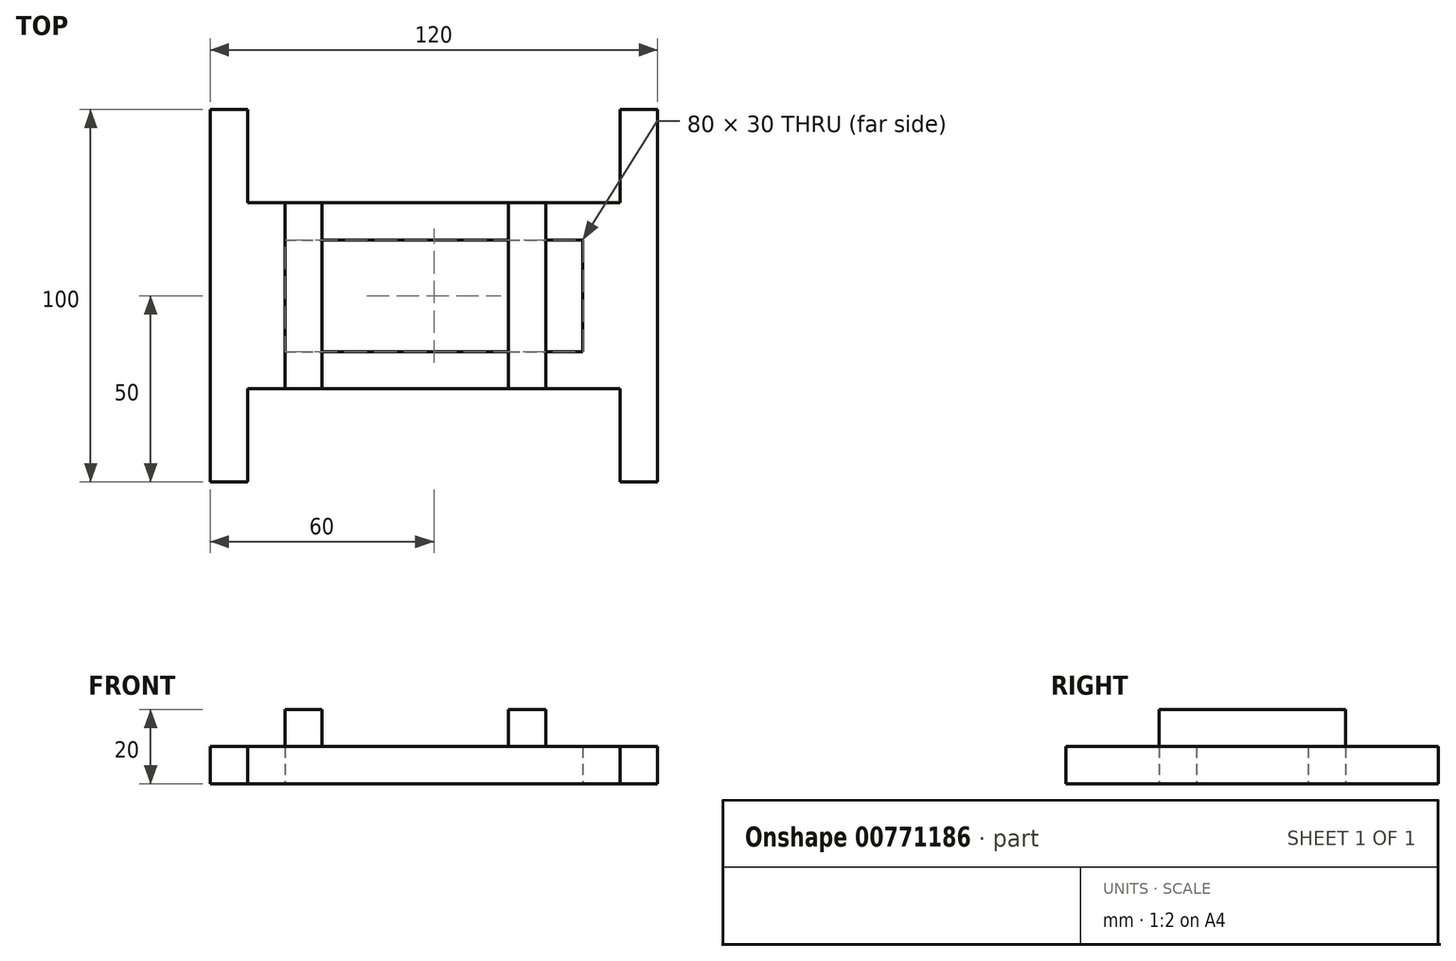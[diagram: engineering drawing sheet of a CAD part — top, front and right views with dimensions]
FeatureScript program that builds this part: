
annotation { "Feature Type Name" : "Feature", "Feature Type Description" : "" }
export const myFeature = defineFeature(function(context is Context, id is Id, definition is map)
    precondition{}
    {
        {
            var Q0;
            Q0=qCreatedBy(makeId("Top.planeOp"),FACE);
            var sketch = newSketch(context, id + "F0", { "sketchPlane" : qUnion([Q0])});
            skLineSegment(sketch, "E0.bottom", {"start": v(-50, 25) * mm, "end": v(50, 25) * mm});
            skLineSegment(sketch, "E0.top", {"start": v(-50, -25) * mm, "end": v(50, -25) * mm});
            skLineSegment(sketch, "E1.bottom", {"start": v(-60, 50) * mm, "end": v(-50, 50) * mm});
            skLineSegment(sketch, "E1.top", {"start": v(-60, -50) * mm, "end": v(-50, -50) * mm});
            skLineSegment(sketch, "E1.left", {"start": v(-60, 50) * mm, "end": v(-60, -50) * mm});
            skLineSegment(sketch, "E1.right", {"start": v(-50, 50) * mm, "end": v(-50, 25) * mm});
            skLineSegment(sketch, "E2.bottom", {"start": v(50, 50) * mm, "end": v(60, 50) * mm});
            skLineSegment(sketch, "E2.top", {"start": v(50, -50) * mm, "end": v(60, -50) * mm});
            skLineSegment(sketch, "E2.left", {"start": v(50, 50) * mm, "end": v(50, 25) * mm});
            skLineSegment(sketch, "E2.right", {"start": v(60, 50) * mm, "end": v(60, -50) * mm});
            skLineSegment(sketch, "E3.bottom", {"start": v(-40, 15) * mm, "end": v(40, 15) * mm});
            skLineSegment(sketch, "E3.top", {"start": v(-40, -15) * mm, "end": v(40, -15) * mm});
            skLineSegment(sketch, "E3.left", {"start": v(-40, 15) * mm, "end": v(-40, -15) * mm});
            skLineSegment(sketch, "E3.right", {"start": v(40, 15) * mm, "end": v(40, -15) * mm});
            skLineSegment(sketch, "E4.trimOffspring", {"start": v(-50, -25) * mm, "end": v(-50, -50) * mm});
            skLineSegment(sketch, "E5.trimOffspring", {"start": v(50, -25) * mm, "end": v(50, -50) * mm});
            skSolve(sketch);
        }
        {
            var Q0;
            Q0 = qSketchRegion(id + "F0", true);
            extrude(context, id + "F1", {"entities" : qUnion([Q0]), "depth" : 10 * mm, "offsetDistance" : 25 * mm});
        }
        {
            var Q0;
            Q0=makeQuery(id+"F1.opExtrude","SWEPT_FACE",FACE,{"disambiguationData":[OSD([sQuery(id+"F0.wireOp",EDGE,"E0.top")])]});
            var sketch = newSketch(context, id + "F2", { "sketchPlane" : qUnion([Q0])});
            skLineSegment(sketch, "E6.top", {"start": v(-50, 10) * mm, "end": v(-40, 10) * mm});
            skLineSegment(sketch, "E7.bottom", {"start": v(20, 20) * mm, "end": v(30, 20) * mm});
            skLineSegment(sketch, "E7.top", {"start": v(20, 10) * mm, "end": v(30, 10) * mm});
            skLineSegment(sketch, "E7.left", {"start": v(20, 20) * mm, "end": v(20, 10) * mm});
            skLineSegment(sketch, "E7.right", {"start": v(30, 20) * mm, "end": v(30, 10) * mm});
            skLineSegment(sketch, "E8.bottom", {"start": v(-40, 20) * mm, "end": v(-30, 20) * mm});
            skLineSegment(sketch, "E8.top", {"start": v(-40, 10) * mm, "end": v(-30, 10) * mm});
            skLineSegment(sketch, "E8.left", {"start": v(-40, 20) * mm, "end": v(-40, 10) * mm});
            skLineSegment(sketch, "E8.right", {"start": v(-30, 20) * mm, "end": v(-30, 10) * mm});
            skSolve(sketch);
        }
        {
            var Q0;
            Q0=makeQuery(id+"F2.imprint","IMPRINT",FACE,{"disambiguationData":[TD([[makeQuery(id+"F2.imprint","IMPRINT",EDGE,{"derivedFrom":sQuery(id+"F2.wireOp",EDGE,"E8.bottom")}),-1.0]])]});
            var Q1;
            Q1=makeQuery(id+"F2.imprint","IMPRINT",FACE,{"disambiguationData":[TD([[makeQuery(id+"F2.imprint","IMPRINT",EDGE,{"derivedFrom":sQuery(id+"F2.wireOp",EDGE,"E7.bottom")}),-1.0]])]});
            extrude(context, id + "F3", {"entities" : qUnion([Q0, Q1]), "oppositeDirection" : true, "depth" : 50 * mm, "offsetDistance" : 25 * mm});
        }
    });
